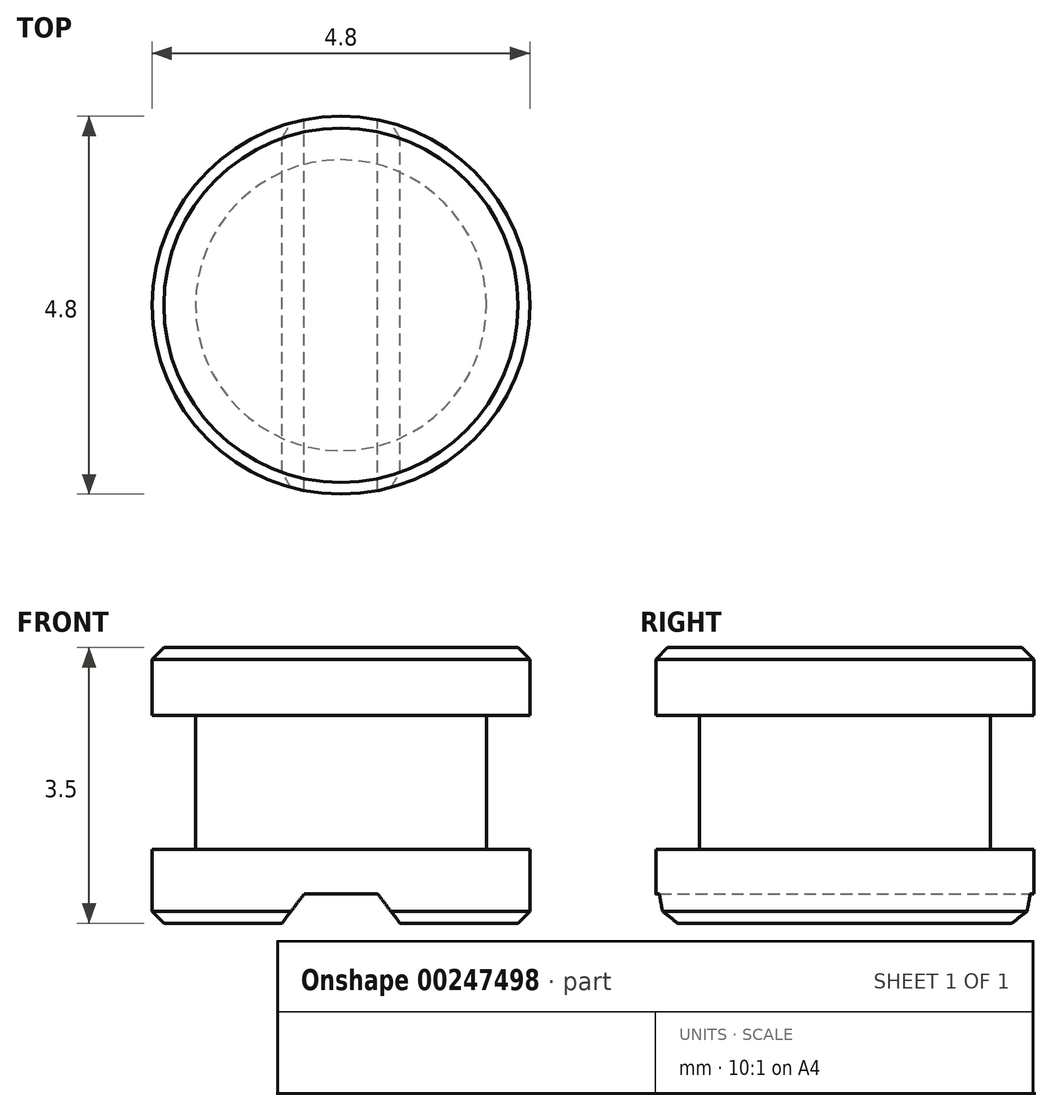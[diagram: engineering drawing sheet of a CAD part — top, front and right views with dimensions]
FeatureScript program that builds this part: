
annotation { "Feature Type Name" : "Feature", "Feature Type Description" : "" }
export const myFeature = defineFeature(function(context is Context, id is Id, definition is map)
    precondition{}
    {
        {
            var Q0;
            Q0=qCreatedBy(makeId("Front.planeOp"),FACE);
            var sketch = newSketch(context, id + "F0", { "sketchPlane" : qUnion([Q0])});
            skLineSegment(sketch, "E0.bottom", {"start": v(0, 0) * mm, "end": v(2.25, 0) * mm});
            skLineSegment(sketch, "E0.top", {"start": v(0, 3.5) * mm, "end": v(2.25, 3.5) * mm});
            skLineSegment(sketch, "E0.left", {"start": v(0, 0) * mm, "end": v(0, 3.5) * mm});
            skLineSegment(sketch, "E0.right", {"start": v(2.4, 0.15) * mm, "end": v(2.4, 0.94) * mm});
            skLineSegment(sketch, "E1", {"start": v(2.25, 3.5) * mm, "end": v(2.4, 3.35) * mm});
            skLineSegment(sketch, "E2", {"start": v(2.4, 2.64) * mm, "end": v(1.85, 2.64) * mm});
            skLineSegment(sketch, "E3", {"start": v(1.85, 2.64) * mm, "end": v(1.85, 0.94) * mm});
            skLineSegment(sketch, "E4", {"start": v(1.85, 0.94) * mm, "end": v(2.4, 0.94) * mm});
            skLineSegment(sketch, "E5.trimOffspring", {"start": v(2.4, 2.64) * mm, "end": v(2.4, 3.35) * mm});
            skLineSegment(sketch, "E6", {"start": v(2.25, 0) * mm, "end": v(2.4, 0.15) * mm});
            skSolve(sketch);
        }
        {
            var Q0;
            Q0=qSketchRegion(id+"F0",true);
            var Q1;
            Q1=sQuery(id+"F0.wireOp",EDGE,"E0.left");
            revolve(context, id + "F1", {"entities" : qUnion([Q0]), "axis" : qUnion([Q1]), "revolveType" : RevolveType.FULL});
        }
        {
            var Q0;
            Q0=qCreatedBy(makeId("Front.planeOp"),FACE);
            var sketch = newSketch(context, id + "F2", { "sketchPlane" : qUnion([Q0])});
            skLineSegment(sketch, "E7", {"start": v(-0.75, 0) * mm, "end": v(-0.47, 0.37) * mm});
            skLineSegment(sketch, "E8", {"start": v(-0.47, 0.37) * mm, "end": v(0, 0.37) * mm});
            skLineSegment(sketch, "E9", {"start": v(-0.75, 0) * mm, "end": v(0, 0) * mm});
            skLineSegment(sketch, "E10", {"start": v(0, 0) * mm, "end": v(0, 0.37) * mm, "construction": true});
            skLineSegment(sketch, "E11.MirrorCS", {"start": v(0.47, 0.37) * mm, "end": v(0, 0.37) * mm});
            skLineSegment(sketch, "E12.MirrorCS", {"start": v(0.75, 0) * mm, "end": v(0, 0) * mm});
            skLineSegment(sketch, "E13.MirrorCS", {"start": v(0.75, 0) * mm, "end": v(0.47, 0.37) * mm});
            skSolve(sketch);
        }
        {
            var Q0;
            Q0=qSketchRegion(id+"F2",true);
            extrude(context, id + "F3", {"entities" : qUnion([Q0]), "operationType" : NewBodyOperationType.REMOVE, "endBound" : BoundingType.THROUGH_ALL, "depth" : 25 * mm, "hasSecondDirection" : true, "secondDirectionBound" : SecondDirectionBoundingType.THROUGH_ALL, "secondDirectionOppositeDirection" : true, "secondDirectionDepth" : 25 * mm});
        }
    });
